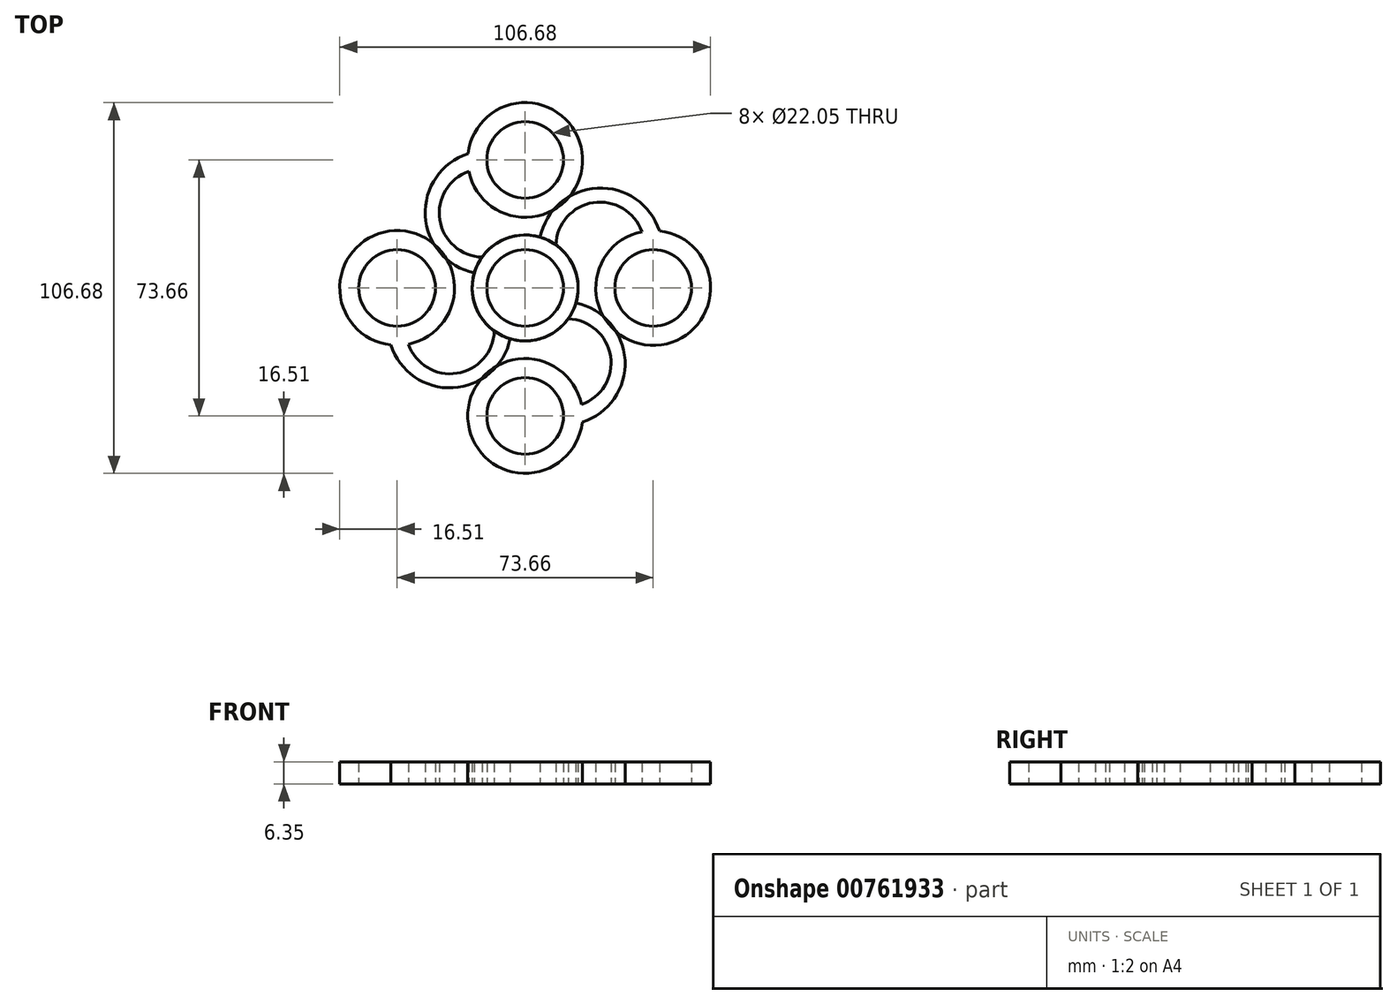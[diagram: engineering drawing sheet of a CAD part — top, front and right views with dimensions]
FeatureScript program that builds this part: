
annotation { "Feature Type Name" : "Feature", "Feature Type Description" : "" }
export const myFeature = defineFeature(function(context is Context, id is Id, definition is map)
    precondition{}
    {
        {
            var Q0;
            Q0=qCreatedBy(makeId("Top.planeOp"),FACE);
            var sketch = newSketch(context, id + "F0", { "sketchPlane" : qUnion([Q0])});
            skCircle(sketch, "E0", {"center": v(0, 0) * mm, "radius": 15.24 * mm});
            skCircle(sketch, "E1", {"center": v(0, 0) * mm, "radius": 11.02 * mm});
            skCircle(sketch, "E2", {"center": v(0, 36.83) * mm, "radius": 11.02 * mm});
            skCircle(sketch, "E3", {"center": v(0, 36.83) * mm, "radius": 16.51 * mm});
            skArc(sketch, "E4", {"start": v(-16.41, 38.63) * mm, "mid": v(-28.72, 20.78) * mm, "end": v(-14.62, 4.3) * mm});
            skArc(sketch, "E5", {"start": v(-16.18, 33.56) * mm, "mid": v(-24.56, 19.64) * mm, "end": v(-12.4, 8.87) * mm});
            skSolve(sketch);
        }
        {
            var Q0;
            Q0=makeQuery(id+"F0.imprint","IMPRINT",FACE,{"disambiguationData":[TD([[makeQuery(id+"F0.imprint","IMPRINT",EDGE,{"derivedFrom":sQuery(id+"F0.wireOp",EDGE,"E2")}),-1.0]])]});
            var Q1;
            {var subQ0=sQuery(id+"F0.wireOp",EDGE,"E4");Q1=makeQuery(id+"F0.imprint","IMPRINT",FACE,{"disambiguationData":[TD([[makeQuery(id+"F0.imprint","IMPRINT",EDGE,{"derivedFrom":subQ0}),1.0]])]});}
            var Q2;
            Q2=makeQuery(id+"F0.imprint","IMPRINT",FACE,{"disambiguationData":[TD([[makeQuery(id+"F0.imprint","IMPRINT",EDGE,{"derivedFrom":sQuery(id+"F0.wireOp",EDGE,"E1")}),-1.0]])]});
            extrude(context, id + "F1", {"entities" : qUnion([Q0, Q1, Q2]), "depth" : 6.35 * mm, "offsetDistance" : 25.4 * mm});
        }
        {
            var Q0;
            Q0=makeQuery(id+"F1.opExtrude","SWEPT_BODY",BODY,{"disambiguationData":[OSD([sQuery(id+"F0.wireOp",EDGE,"E0"),sQuery(id+"F0.wireOp",EDGE,"E1"),sQuery(id+"F0.wireOp",EDGE,"E2"),sQuery(id+"F0.wireOp",EDGE,"E3"),sQuery(id+"F0.wireOp",EDGE,"E4"),sQuery(id+"F0.wireOp",EDGE,"E5")])]});
            var Q1;
            Q1=makeQuery(id+"F1.opExtrude","CAP_EDGE",EDGE,{"disambiguationData":[OSD([sQuery(id+"F0.wireOp",EDGE,"E1")])],"isStart":false});
            circularPattern(context, id + "F2", {"entities" : qUnion([Q0]), "axis" : qUnion([Q1]), "angle" : 360 * degree, "instanceCount" : 4, "equalSpace" : true});
        }
    });
